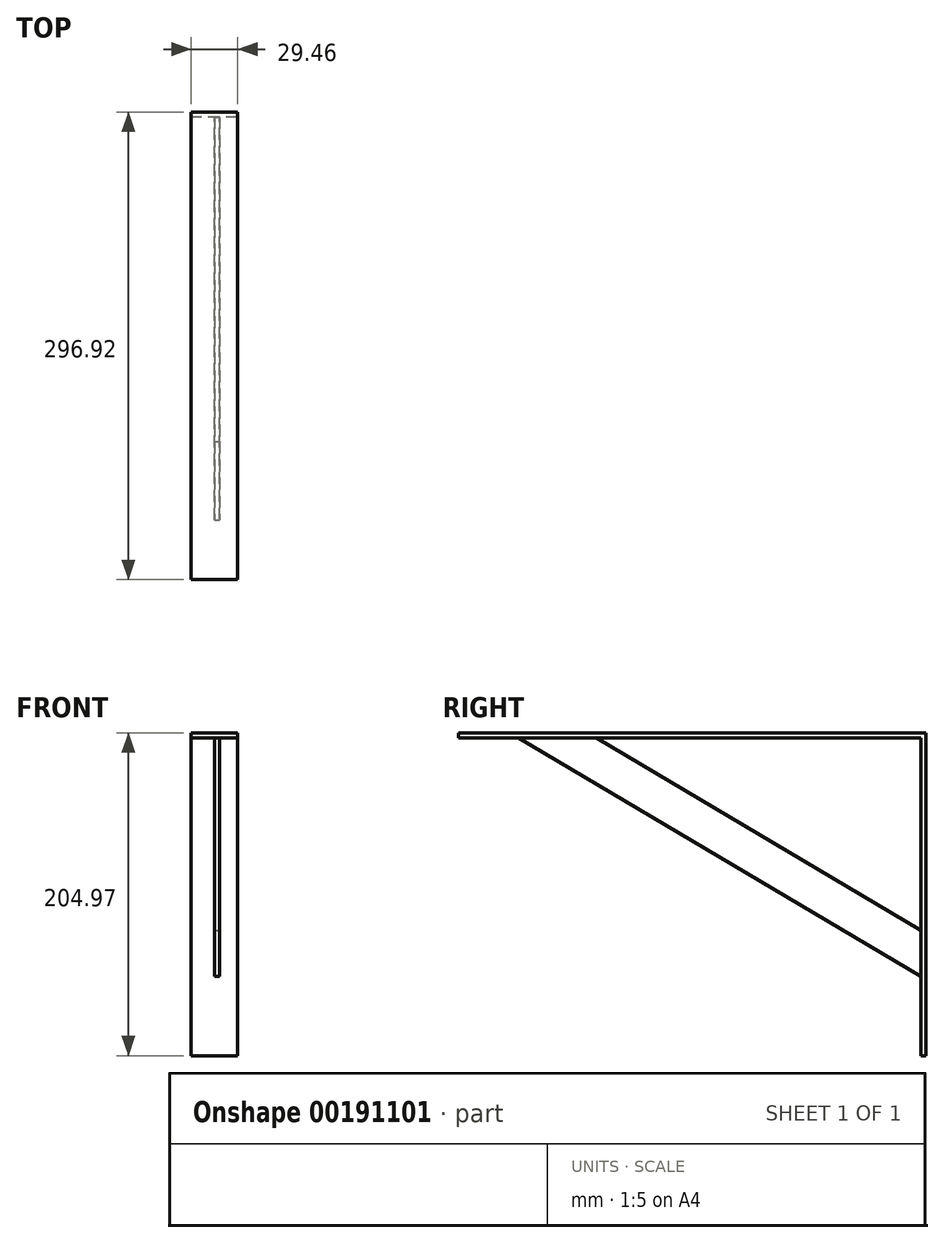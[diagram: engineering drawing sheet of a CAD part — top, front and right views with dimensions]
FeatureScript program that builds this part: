
annotation { "Feature Type Name" : "Feature", "Feature Type Description" : "" }
export const myFeature = defineFeature(function(context is Context, id is Id, definition is map)
    precondition{}
    {
        {
            var Q0;
            Q0=qCreatedBy(makeId("Top.planeOp"),FACE);
            var sketch = newSketch(context, id + "F0", { "sketchPlane" : qUnion([Q0])});
            skLineSegment(sketch, "E0.bottom", {"start": v(-14.73, 148.46) * mm, "end": v(14.73, 148.46) * mm});
            skLineSegment(sketch, "E0.top", {"start": v(-14.73, -148.46) * mm, "end": v(14.73, -148.46) * mm});
            skLineSegment(sketch, "E0.left", {"start": v(-14.73, 148.46) * mm, "end": v(-14.73, -148.46) * mm});
            skLineSegment(sketch, "E0.right", {"start": v(14.73, 148.46) * mm, "end": v(14.73, -148.46) * mm});
            skPoint(sketch, "E0.middle", {"position": v(0, 0) * mm});
            skSolve(sketch);
        }
        {
            var Q0;
            Q0 = qSketchRegion(id + "F0", true);
            extrude(context, id + "F1", {"entities" : qUnion([Q0]), "depth" : 3.17 * mm});
        }
        {
            var Q0;
            Q0=makeQuery(id+"F1.opExtrude","SWEPT_FACE",FACE,{"disambiguationData":[OSD([sQuery(id+"F0.wireOp",EDGE,"E0.bottom")])]});
            var sketch = newSketch(context, id + "F2", { "sketchPlane" : qUnion([Q0])});
            skLineSegment(sketch, "E1.bottom", {"start": v(-14.73, 3.18) * mm, "end": v(14.73, 3.18) * mm});
            skLineSegment(sketch, "E1.top", {"start": v(-14.73, -201.8) * mm, "end": v(14.73, -201.8) * mm});
            skLineSegment(sketch, "E1.left", {"start": v(-14.73, 3.18) * mm, "end": v(-14.73, -201.8) * mm});
            skLineSegment(sketch, "E1.right", {"start": v(14.73, 3.18) * mm, "end": v(14.73, -201.8) * mm});
            skSolve(sketch);
        }
        {
            var Q0;
            Q0 = qSketchRegion(id + "F2", true);
            extrude(context, id + "F3", {"entities" : qUnion([Q0]), "operationType" : NewBodyOperationType.ADD, "oppositeDirection" : true, "depth" : 3.17 * mm});
        }
        {
            var Q0;
            Q0=qCreatedBy(makeId("Right.planeOp"),FACE);
            cPlane(context, id + "F4", {"entities" : qUnion([Q0]), "cplaneType" : CPlaneType.OFFSET, "offset" : 3.17 * mm, "width" : 152.4 * mm, "height" : 152.4 * mm});
        }
        {
            var Q0;
            Q0=qCreatedBy(id+"F4.planeOp",FACE);
            var sketch = newSketch(context, id + "F5", { "sketchPlane" : qUnion([Q0])});
            skLineSegment(sketch, "E2", {"start": v(145.29, 0) * mm, "end": v(-170.69, 0) * mm, "construction": true});
            skLineSegment(sketch, "E3", {"start": v(145.29, 0) * mm, "end": v(145.29, -207.89) * mm, "construction": true});
            skLineSegment(sketch, "E4", {"start": v(145.29, -122.11) * mm, "end": v(-60.82, 0) * mm});
            skLineSegment(sketch, "E5", {"start": v(-60.82, 0) * mm, "end": v(-110.56, 0) * mm});
            skLineSegment(sketch, "E6", {"start": v(-110.56, 0) * mm, "end": v(145.29, -151.58) * mm});
            skLineSegment(sketch, "E7", {"start": v(145.29, -151.58) * mm, "end": v(145.29, -122.11) * mm});
            skSolve(sketch);
        }
        {
            var Q0;
            Q0 = qSketchRegion(id + "F5", true);
            extrude(context, id + "F6", {"entities" : qUnion([Q0]), "operationType" : NewBodyOperationType.ADD, "oppositeDirection" : true, "depth" : 3.17 * mm});
        }
    });
